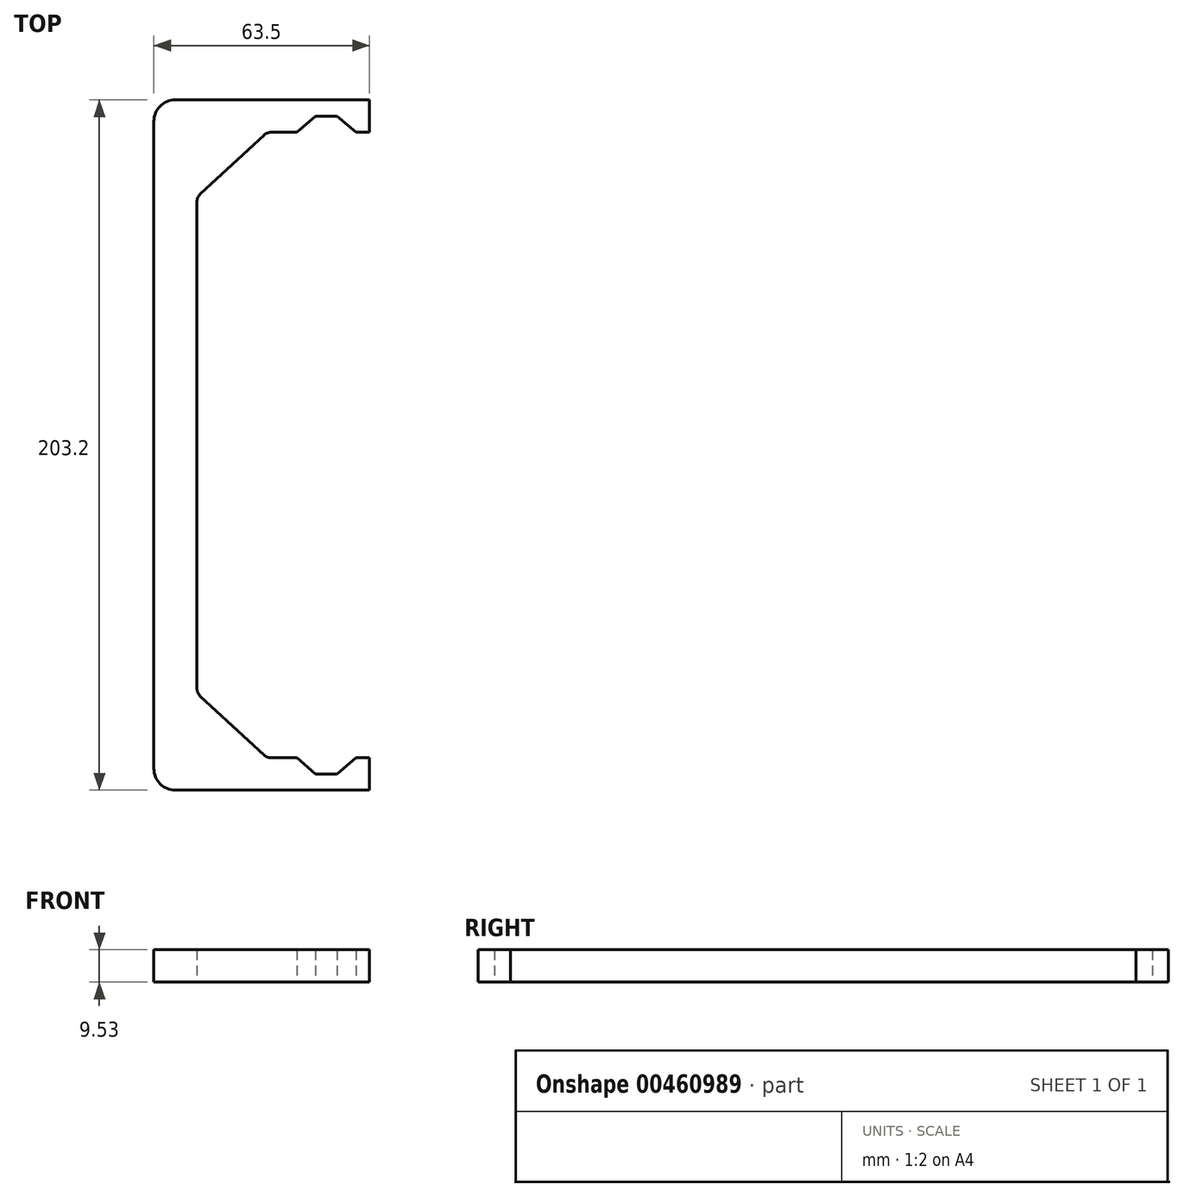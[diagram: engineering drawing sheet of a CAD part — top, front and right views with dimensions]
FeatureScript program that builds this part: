
annotation { "Feature Type Name" : "Feature", "Feature Type Description" : "" }
export const myFeature = defineFeature(function(context is Context, id is Id, definition is map)
    precondition{}
    {
        {
            var Q0;
            Q0=qCreatedBy(makeId("Top.planeOp"),FACE);
            var sketch = newSketch(context, id + "F0", { "sketchPlane" : qUnion([Q0])});
            skLineSegment(sketch, "E0.bottom", {"start": v(-46.74, 147.98) * mm, "end": v(-2.29, 147.98) * mm});
            skLineSegment(sketch, "E0.top", {"start": v(-46.74, -55.22) * mm, "end": v(-2.29, -55.22) * mm});
            skLineSegment(sketch, "E0.left", {"start": v(-53.09, 141.63) * mm, "end": v(-53.09, -48.87) * mm});
            skLineSegment(sketch, "E1.0", {"start": v(-40.39, 118.01) * mm, "end": v(-40.39, -25.26) * mm});
            skLineSegment(sketch, "E2.0", {"start": v(-18.5, 138.45) * mm, "end": v(-11, 138.45) * mm});
            skLineSegment(sketch, "E3", {"start": v(-20.66, 137.61) * mm, "end": v(-39.36, 120.35) * mm});
            skLineSegment(sketch, "E4", {"start": v(-39.36, -27.59) * mm, "end": v(-20.66, -44.85) * mm});
            skPoint(sketch, "E5.orphan", {"position": v(-2.29, 147.98) * mm});
            skPoint(sketch, "E6.visualSharp", {"position": v(-53.09, 147.98) * mm});
            skArc(sketch, "E6.filletArc", {"start": v(-46.74, 147.98) * mm, "mid": v(-51.23, 146.12) * mm, "end": v(-53.09, 141.63) * mm});
            skArc(sketch, "E7.filletArc", {"start": v(-53.09, -48.87) * mm, "mid": v(-51.23, -53.36) * mm, "end": v(-46.74, -55.22) * mm});
            skPoint(sketch, "E8.orphan", {"position": v(10.41, 147.98) * mm});
            skPoint(sketch, "E9.start.orphan", {"position": v(-53.09, 46.38) * mm});
            skPoint(sketch, "E10.orphan", {"position": v(6.43, 138.45) * mm});
            skPoint(sketch, "E11.visualSharp", {"position": v(10.41, 143.22) * mm});
            skPoint(sketch, "E12.visualSharp", {"position": v(-40.39, 119.4) * mm});
            skArc(sketch, "E12.filletArc", {"start": v(-39.36, 120.35) * mm, "mid": v(-40.12, 119.29) * mm, "end": v(-40.39, 118.01) * mm});
            skPoint(sketch, "E13.visualSharp", {"position": v(-19.75, 138.45) * mm});
            skArc(sketch, "E13.filletArc", {"start": v(-18.5, 138.45) * mm, "mid": v(-19.66, 138.24) * mm, "end": v(-20.66, 137.61) * mm});
            skPoint(sketch, "E14.visualSharp", {"position": v(-40.39, -26.65) * mm});
            skArc(sketch, "E14.filletArc", {"start": v(-40.39, -25.26) * mm, "mid": v(-40.12, -26.53) * mm, "end": v(-39.36, -27.59) * mm});
            skPoint(sketch, "E15.visualSharp", {"position": v(-19.75, -45.7) * mm});
            skArc(sketch, "E15.filletArc", {"start": v(-20.66, -44.85) * mm, "mid": v(-19.66, -45.48) * mm, "end": v(-18.5, -45.7) * mm});
            skLineSegment(sketch, "E16", {"start": v(-2.29, 147.98) * mm, "end": v(10.41, 147.98) * mm});
            skLineSegment(sketch, "E17", {"start": v(10.41, 138.45) * mm, "end": v(10.41, 147.98) * mm});
            skLineSegment(sketch, "E18", {"start": v(10.41, 138.45) * mm, "end": v(6.43, 138.45) * mm});
            skPoint(sketch, "E19", {"position": v(-11, 138.45) * mm});
            skLineSegment(sketch, "E20", {"start": v(-5.46, 143.22) * mm, "end": v(0.89, 143.22) * mm});
            skPoint(sketch, "E21", {"position": v(-5.46, 143.22) * mm});
            skPoint(sketch, "E22", {"position": v(0.89, 143.22) * mm});
            skLineSegment(sketch, "E23", {"start": v(-11, 138.45) * mm, "end": v(-5.46, 143.22) * mm});
            skLineSegment(sketch, "E24", {"start": v(0.89, 143.22) * mm, "end": v(6.43, 138.45) * mm});
            skPoint(sketch, "E25.MirrorCS.start.orphan", {"position": v(-2.29, -55.22) * mm});
            skLineSegment(sketch, "E26.MirrorCS", {"start": v(-2.29, -55.22) * mm, "end": v(10.41, -55.22) * mm});
            skLineSegment(sketch, "E27.MirrorCS", {"start": v(10.41, -45.7) * mm, "end": v(10.41, -55.22) * mm});
            skLineSegment(sketch, "E28.MirrorCS", {"start": v(10.41, -45.7) * mm, "end": v(6.43, -45.7) * mm});
            skLineSegment(sketch, "E29.MirrorCS", {"start": v(0.89, -50.46) * mm, "end": v(6.43, -45.7) * mm});
            skLineSegment(sketch, "E30.MirrorCS", {"start": v(-5.46, -50.46) * mm, "end": v(0.89, -50.46) * mm});
            skLineSegment(sketch, "E31.MirrorCS", {"start": v(-11, -45.7) * mm, "end": v(-5.46, -50.46) * mm});
            skLineSegment(sketch, "E32.MirrorCS", {"start": v(-18.5, -45.7) * mm, "end": v(-11, -45.7) * mm});
            skSolve(sketch);
        }
        {
            var Q0;
            Q0=makeQuery(id+"F0.imprint","IMPRINT",FACE,{"disambiguationData":[TD([[makeQuery(id+"F0.imprint","IMPRINT",EDGE,{"derivedFrom":sQuery(id+"F0.wireOp",EDGE,"E0.bottom")}),-1.0]])]});
            extrude(context, id + "F1", {"entities" : qUnion([Q0]), "depth" : 9.52 * mm, "offsetDistance" : 25.4 * mm});
        }
    });
